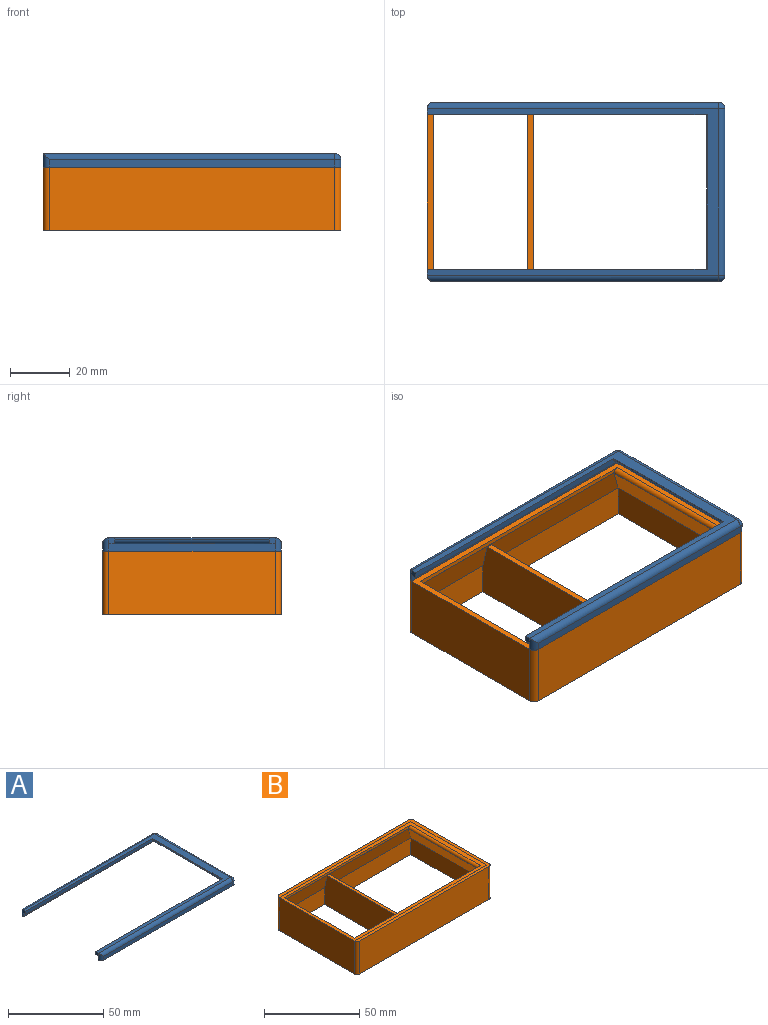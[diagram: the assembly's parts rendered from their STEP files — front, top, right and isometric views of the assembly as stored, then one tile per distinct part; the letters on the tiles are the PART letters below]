
ASSEMBLY  parts=2 mates=1
PART A: 29 faces, bbox 100x60x4.5 mm
  f0: plane 56x3.47mm, normal (-1,0,0), area 153.5mm2, adj f4,f5,f10,f16,f24,f25,f26,f28
  f1: plane 96x2.47mm, normal (0,-1,0), area 237.4mm2, adj f8,f9,f21,f28
  f2: plane 56x2.47mm, normal (1,0,0), area 138.5mm2, adj f6,f8,f19,f28
  f3: plane 96x2.47mm, normal (0,1,0), area 237.4mm2, adj f6,f7,f17,f28
  f4: plane 98x2.47mm, normal (0,-1,0), area 242.4mm2, adj f0,f7,f16,f28
  f5: plane 98x2.47mm, normal (0,1,0), area 242.4mm2, adj f0,f9,f10,f28
  f6: cylinder r=2mm len=2.47mm, axis (0,0,1), area 7.8mm2, adj f2,f3,f18,f28
  f7: cylinder r=2mm len=4.47mm, axis (0,0,-1), area 11.8mm2, adj f3,f4,f12,f17,f28
  f8: cylinder r=2mm len=2.47mm, axis (0,0,-1), area 7.8mm2, adj f1,f2,f20,f28
  f9: cylinder r=2mm len=4.47mm, axis (0,0,1), area 11.8mm2, adj f1,f5,f11,f21,f28
  f10: plane 98x20.5mm, normal (0,0,-1), area 242.2mm2, adj f0,f5,f11,f14,f23,f24
  f11: plane 2x2mm, normal (-1,0,0), area 4mm2, adj f9,f10,f14,f15
  f12: plane 2x2mm, normal (-1,0,0), area 4mm2, adj f7,f13,f15,f16
  f13: plane 95.5x2mm, normal (0,-1,0), area 188.5mm2, adj f12,f15,f16,f22,f23
  f14: plane 95.5x2mm, normal (0,1,0), area 188.5mm2, adj f10,f11,f15,f22,f23
  f15: plane 98x56mm, normal (0,0,1), area 600mm2, adj f11,f12,f13,f14,f17,f19,f21,f22
  f16: plane 98x20.5mm, normal (0,0,-1), area 242.3mm2, adj f0,f4,f12,f13,f23,f25
  f17: cylinder r=2mm len=98mm, axis (1,0,0), area 305.6mm2, adj f3,f7,f15,f18
  f18: sphere r=2mm, area 6.3mm2, adj f6,f17,f19
  f19: cylinder r=2mm len=56mm, axis (0,-1,0), area 175.9mm2, adj f2,f15,f18,f20
  f20: sphere r=2mm, area 6.3mm2, adj f8,f19,f21
  f21: cylinder r=2mm len=98mm, axis (-1,0,0), area 305.6mm2, adj f1,f9,f15,f20
  f22: plane 52x0.5mm, normal (-1,0,0), area 26mm2, adj f13,f14,f15,f23
  f23: cylinder r=1.5mm len=52mm, axis (0,-1,0), area 118.4mm2, adj f10,f13,f14,f16,f22,f24,f25,f27
  f24: plane 2.78x1mm, normal (0,1,0), area 2.2mm2, adj f0,f10,f23,f26,f27
  f25: plane 2.78x1mm, normal (0,-1,0), area 2.2mm2, adj f0,f16,f23,f26,f27
  f26: plane 15x2mm, normal (0,0,-1), area 30mm2, adj f0,f24,f25,f27
  f27: cylinder r=1mm len=15mm, axis (0,-1,0), area 20.2mm2, adj f23,f24,f25,f26
  f28: plane 100x60mm, normal (0,0,-1), area 508.6mm2, adj f0,f1,f2,f3,f4,f5,f6,f7
PART B: 32 faces, bbox 100x60x21.2 mm
  f0: plane 56x21.17mm, normal (1,0,0), area 1161.6mm2, adj f3,f6,f15,f17,f20,f21,f22,f28
  f1: plane 56x19.37mm, normal (1,0,0), area 1068mm2, adj f2,f5,f17,f26,f30,f31
  f2: plane 62.23x10.67mm, normal (0,1,0), area 664mm2, adj f1,f4,f30,f31
  f3: plane 31.77x10.67mm, normal (0,1,0), area 339mm2, adj f0,f14,f30,f31
  f4: plane 56x10.67mm, normal (-1,0,0), area 597.5mm2, adj f2,f5,f16,f31
  f5: plane 62.23x10.67mm, normal (0,-1,0), area 664mm2, adj f1,f4,f17,f31
  f6: plane 31.77x10.67mm, normal (0,-1,0), area 339mm2, adj f0,f14,f17,f31
  f7: plane 56x21.17mm, normal (-1,0,0), area 1185.5mm2, adj f11,f13,f22,f31
  f8: plane 56x21.2mm, normal (1,0,0), area 1187mm2, adj f10,f12,f27,f31
  f9: plane 96x21.2mm, normal (0,1,0), area 2034.9mm2, adj f10,f11,f27,f31
  f10: cylinder r=2mm len=21.2mm, axis (0,0,1), area 66.6mm2, adj f8,f9,f27,f31
  f11: cylinder r=2mm len=21.2mm, axis (0,0,-1), area 66.6mm2, adj f7,f9,f23,f27,f31
  f12: cylinder r=2mm len=21.2mm, axis (0,0,-1), area 66.6mm2, adj f8,f19,f27,f31
  f13: cylinder r=2mm len=21.2mm, axis (0,0,1), area 66.6mm2, adj f7,f19,f24,f27,f31
  f14: plane 56x19.37mm, normal (-1,0,0), area 1068mm2, adj f3,f6,f17,f26,f30,f31
  f15: plane 91.99x0.07mm, normal (0,0,-1), area 6.2mm2, adj f0,f16,f21,f30
  f16: plane 56x9mm, normal (-0.91,0,-0.41), area 532.3mm2, adj f4,f15,f17,f29,f30
  f17: plane 96x9.02mm, normal (0,-0.98,-0.22), area 851.4mm2, adj f0,f1,f5,f6,f14,f16,f25,f26
  f18: plane 56x0.03mm, normal (-1,0,0), area 1.5mm2, adj f22,f23,f24,f27
  f19: plane 96x21.2mm, normal (0,-1,0), area 2034.9mm2, adj f12,f13,f27,f31
  f20: plane 93.5x1.48mm, normal (0,-1,0), area 136.7mm2, adj f0,f22,f25,f28
  f21: plane 93.5x1.5mm, normal (0,1,0), area 138.5mm2, adj f0,f15,f22,f25,f29
  f22: plane 98x56mm, normal (0,0,1), area 626mm2, adj f0,f7,f18,f20,f21,f23,f24,f25
  f23: plane 98x0.03mm, normal (0,-1,0), area 2.6mm2, adj f11,f18,f22,f27
  f24: plane 98x0.03mm, normal (0,1,0), area 2.6mm2, adj f13,f18,f22,f27
  f25: cylinder r=1.5mm len=52mm, axis (0,1,0), area 122.5mm2, adj f17,f20,f21,f22,f28,f29
  f26: plane 52.16x2mm, normal (0,0,1), area 104.3mm2, adj f1,f14,f17,f30
  f27: plane 100x60mm, normal (0,0,1), area 508.6mm2, adj f8,f9,f10,f11,f12,f13,f18,f19
  f28: plane 92x0.04mm, normal (0,0,1), area 3.9mm2, adj f0,f17,f20,f25
  f29: plane 51.96x0.01mm, normal (0,0,1), area 0.7mm2, adj f16,f17,f21,f25
  f30: plane 96x9mm, normal (0,0.98,-0.21), area 847.4mm2, adj f0,f1,f2,f3,f14,f15,f16,f26
  f31: plane 100x60mm, normal (0,0,-1), area 732.6mm2, adj f0,f1,f2,f3,f4,f5,f6,f7
PLACE A t=(-0.98,-2.97,-23.86)mm
PLACE B t=(-0.98,-2.97,-23.86)mm
MATE fastened A.f28 <-> B.f27  axis (0,0,-1) through (49.02,25.03,16.67)mm
